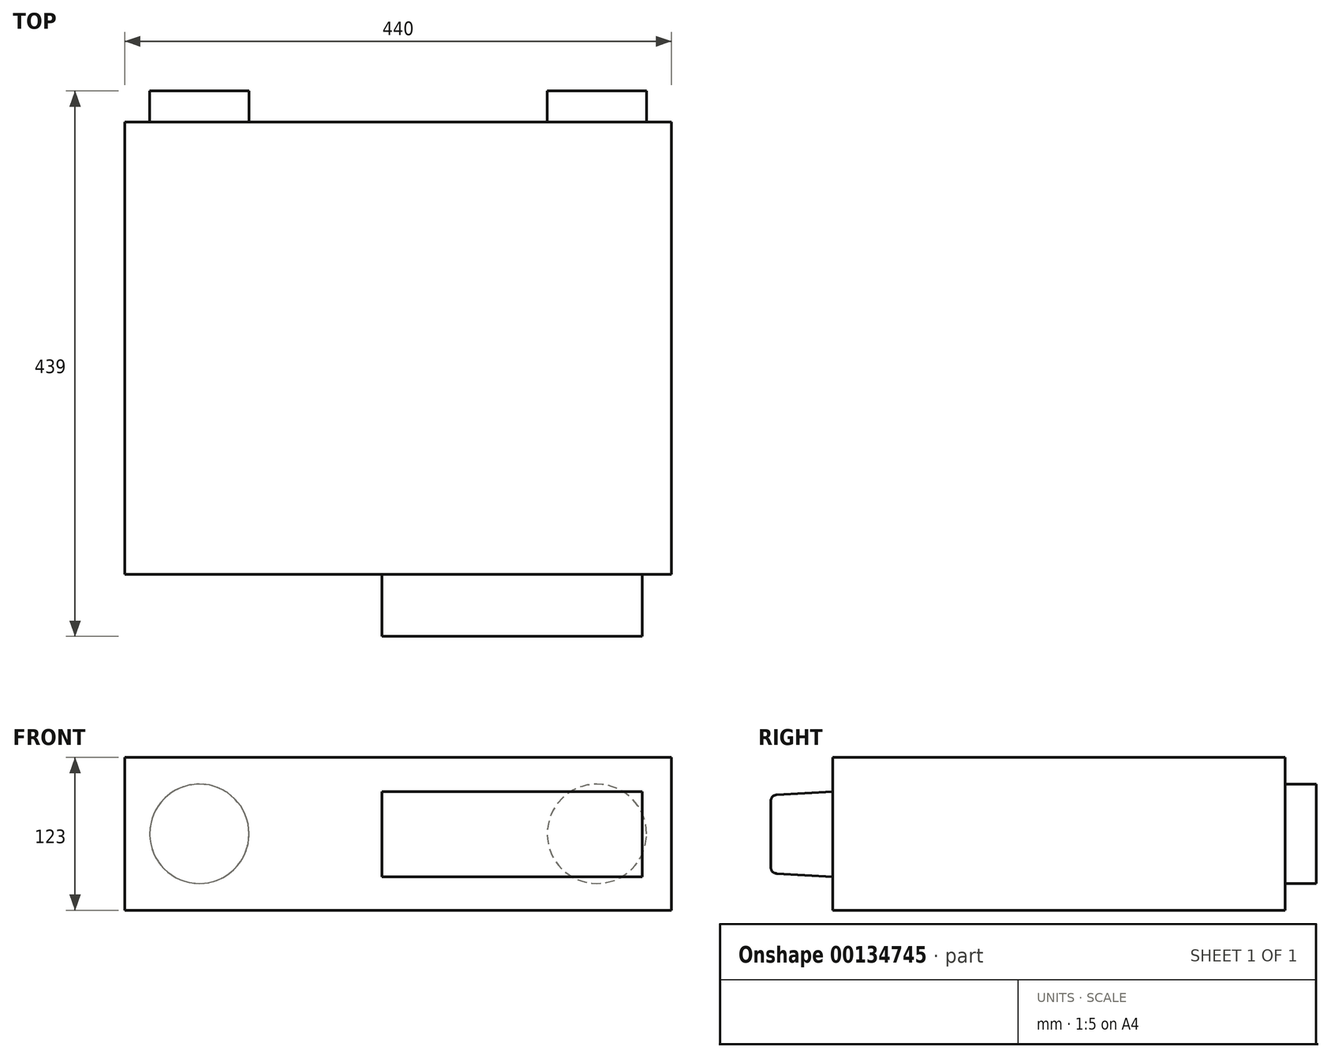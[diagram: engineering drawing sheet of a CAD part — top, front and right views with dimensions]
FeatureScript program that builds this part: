
annotation { "Feature Type Name" : "Feature", "Feature Type Description" : "" }
export const myFeature = defineFeature(function(context is Context, id is Id, definition is map)
    precondition{}
    {
        {
            var Q0;
            Q0=qCreatedBy(makeId("Front.planeOp"),FACE);
            var sketch = newSketch(context, id + "F0", { "sketchPlane" : qUnion([Q0])});
            skLineSegment(sketch, "E0.bottom", {"start": v(-220, 61.5) * mm, "end": v(220, 61.5) * mm});
            skLineSegment(sketch, "E0.top", {"start": v(-220, -61.5) * mm, "end": v(220, -61.5) * mm});
            skLineSegment(sketch, "E0.left", {"start": v(-220, 61.5) * mm, "end": v(-220, -61.5) * mm});
            skLineSegment(sketch, "E0.right", {"start": v(220, 61.5) * mm, "end": v(220, -61.5) * mm});
            skSolve(sketch);
        }
        {
            var Q0;
            Q0=makeQuery(id+"F0.imprint","IMPRINT",FACE,{"disambiguationData":[TD([[makeQuery(id+"F0.imprint","IMPRINT",EDGE,{"derivedFrom":sQuery(id+"F0.wireOp",EDGE,"E0.bottom")}),-1.0]])]});
            extrude(context, id + "F1", {"entities" : qUnion([Q0]), "depth" : 364 * mm});
        }
        {
            var Q0;
            Q0=makeQuery(id+"F1.opExtrude","CAP_FACE",FACE,{"disambiguationData":[OSD([sQuery(id+"F0.wireOp",EDGE,"E0.bottom"),sQuery(id+"F0.wireOp",EDGE,"E0.top"),sQuery(id+"F0.wireOp",EDGE,"E0.left"),sQuery(id+"F0.wireOp",EDGE,"E0.right")])],"isStart":true});
            var sketch = newSketch(context, id + "F2", { "sketchPlane" : qUnion([Q0])});
            skCircle(sketch, "E1", {"center": v(-160, 0) * mm, "radius": 40 * mm});
            skCircle(sketch, "E2", {"center": v(160, 0) * mm, "radius": 40 * mm});
            skSolve(sketch);
        }
        {
            var Q0;
            Q0 = qSketchRegion(id + "F2", true);
            extrude(context, id + "F3", {"entities" : qUnion([Q0]), "operationType" : NewBodyOperationType.ADD, "depth" : 25 * mm});
        }
        {
            var Q0;
            Q0=makeQuery(id+"F1.opExtrude","CAP_FACE",FACE,{"disambiguationData":[OSD([sQuery(id+"F0.wireOp",EDGE,"E0.bottom"),sQuery(id+"F0.wireOp",EDGE,"E0.top"),sQuery(id+"F0.wireOp",EDGE,"E0.left"),sQuery(id+"F0.wireOp",EDGE,"E0.right")])],"isStart":false});
            var sketch = newSketch(context, id + "F4", { "sketchPlane" : qUnion([Q0])});
            skLineSegment(sketch, "E3.bottom", {"start": v(-13, 34.04) * mm, "end": v(196.38, 34.04) * mm});
            skLineSegment(sketch, "E3.top", {"start": v(-13, -34.72) * mm, "end": v(196.38, -34.72) * mm});
            skLineSegment(sketch, "E3.left", {"start": v(-13, 34.04) * mm, "end": v(-13, -34.72) * mm});
            skLineSegment(sketch, "E3.right", {"start": v(196.38, 34.04) * mm, "end": v(196.38, -34.72) * mm});
            skSolve(sketch);
        }
        {
            var Q0;
            Q0 = qSketchRegion(id + "F4", true);
            extrude(context, id + "F5", {"entities" : qUnion([Q0]), "operationType" : NewBodyOperationType.ADD, "depth" : 50 * mm});
        }
        {
            var Q0;
            Q0=makeQuery(id+"F5.opExtrude","CAP_EDGE",EDGE,{"disambiguationData":[OSD([sQuery(id+"F4.wireOp",EDGE,"E3.bottom")])],"isStart":false});
            var Q1;
            Q1=makeQuery(id+"F5.opExtrude","CAP_EDGE",EDGE,{"disambiguationData":[OSD([sQuery(id+"F4.wireOp",EDGE,"E3.top")])],"isStart":false});
            chamfer(context, id + "F6", {"entities" : qUnion([Q0, Q1]), "chamferType" : ChamferType.TWO_OFFSETS, "width1" : 50 * mm, "oppositeDirection" : false, "width2" : 3 * mm, "tangentPropagation" : true});
        }
        {
            var Q0;
            {var subQ0=sQuery(id+"F4.wireOp",EDGE,"E3.bottom");Q0=makeQuery(id+"F6.opChamfer","BLEND_EDGE",EDGE,{"blendedFrom":[makeQuery(id+"F5.opExtrude","CAP_EDGE",EDGE,{"disambiguationData":[OSD([subQ0])],"isStart":false}),makeQuery(id+"F5.opExtrude","CAP_FACE",FACE,{"disambiguationData":[OSD([subQ0,sQuery(id+"F4.wireOp",EDGE,"E3.top"),sQuery(id+"F4.wireOp",EDGE,"E3.left"),sQuery(id+"F4.wireOp",EDGE,"E3.right")])],"isStart":false})],"blendedInto":[makeQuery(id+"F5.opExtrude","CAP_FACE",FACE,{"disambiguationData":[OSD([subQ0,sQuery(id+"F4.wireOp",EDGE,"E3.top"),sQuery(id+"F4.wireOp",EDGE,"E3.left"),sQuery(id+"F4.wireOp",EDGE,"E3.right")])],"isStart":false})]});}
            var Q1;
            {var subQ0=sQuery(id+"F4.wireOp",EDGE,"E3.top");Q1=makeQuery(id+"F6.opChamfer","BLEND_EDGE",EDGE,{"blendedFrom":[makeQuery(id+"F5.opExtrude","CAP_EDGE",EDGE,{"disambiguationData":[OSD([subQ0])],"isStart":false}),makeQuery(id+"F5.opExtrude","CAP_FACE",FACE,{"disambiguationData":[OSD([sQuery(id+"F4.wireOp",EDGE,"E3.bottom"),subQ0,sQuery(id+"F4.wireOp",EDGE,"E3.left"),sQuery(id+"F4.wireOp",EDGE,"E3.right")])],"isStart":false})],"blendedInto":[makeQuery(id+"F5.opExtrude","CAP_FACE",FACE,{"disambiguationData":[OSD([sQuery(id+"F4.wireOp",EDGE,"E3.bottom"),subQ0,sQuery(id+"F4.wireOp",EDGE,"E3.left"),sQuery(id+"F4.wireOp",EDGE,"E3.right")])],"isStart":false})]});}
            fillet(context, id + "F7", {"entities" : qUnion([Q0, Q1]), "radius" : 5 * mm, "tangentPropagation" : true, "allowEdgeOverflow" : false});
        }
    });
